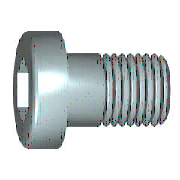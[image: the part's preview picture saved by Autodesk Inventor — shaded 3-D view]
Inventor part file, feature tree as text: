
AUTODESK INVENTOR PART (.ipt)
format: ipt  version: 2024 (Build 280153000, 153)  size: 192,512 bytes
history: native  units: mm (DEFAULTED — no unit token found)
features: other x3, extrude x1, plane x1
ambient origin geometry x7: Origin, YZ Plane, XY Plane, X Axis, Y Axis, Z Axis, Center Point
bodies: Solid1 (feature_tree)
feature tree (5):
  other  "Базовый элемент"
  other  "Фаска2"
  extrude  "Паз"  Depth=2.8mm
  other  "Work Axis1"
  plane  "Work Plane1"
